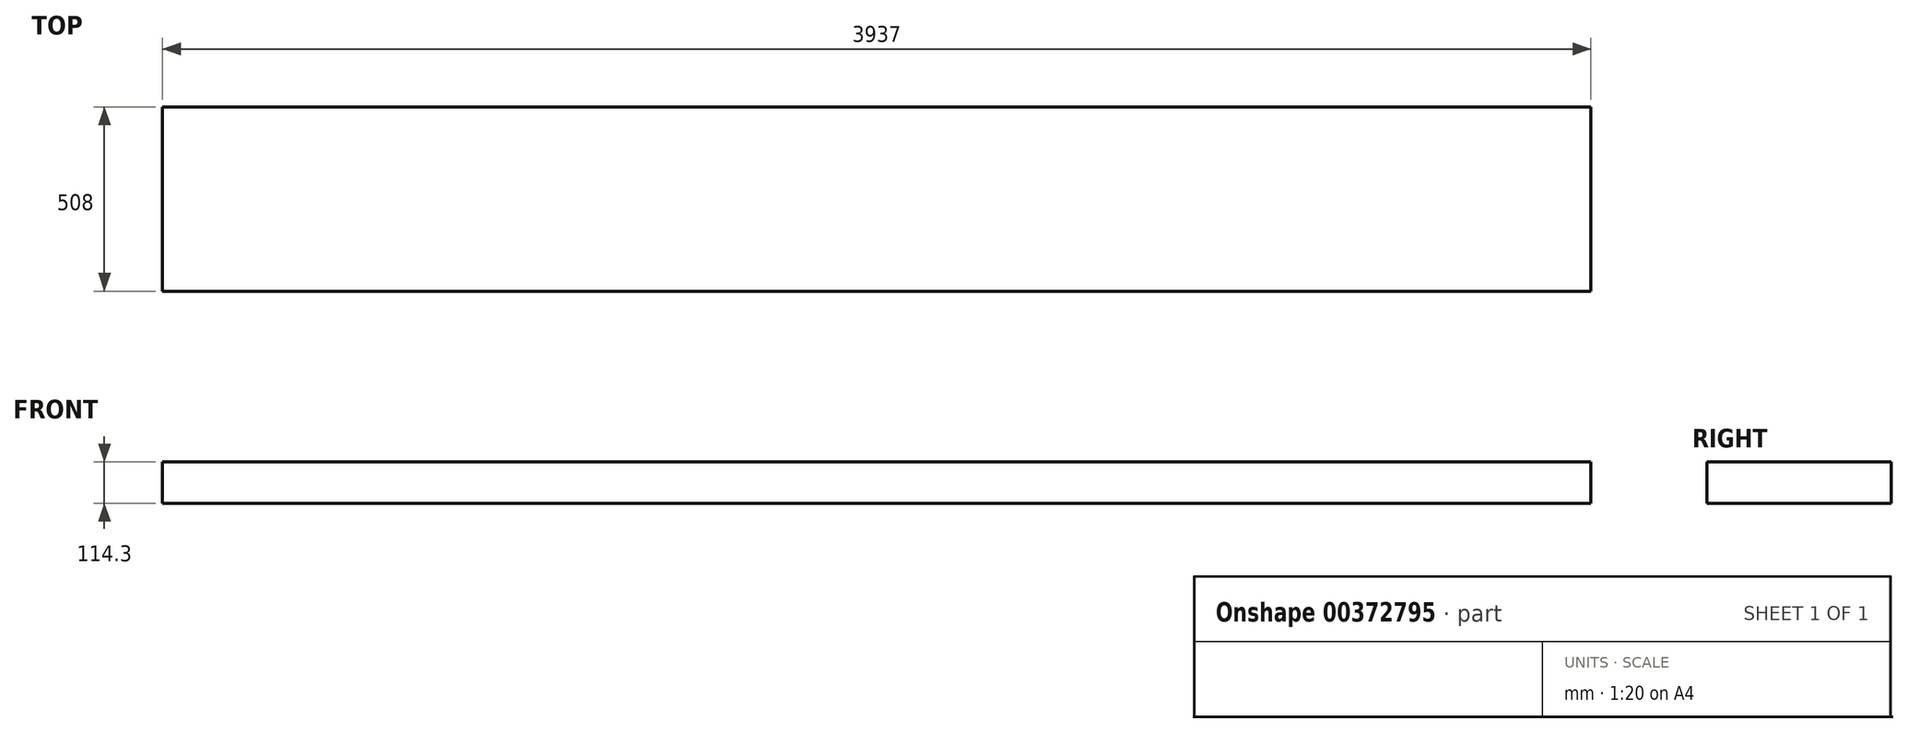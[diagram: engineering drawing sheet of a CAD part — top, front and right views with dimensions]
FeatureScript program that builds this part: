
annotation { "Feature Type Name" : "Feature", "Feature Type Description" : "" }
export const myFeature = defineFeature(function(context is Context, id is Id, definition is map)
    precondition{}
    {
        {
            var Q0;
            Q0=qCreatedBy(makeId("Top.planeOp"),FACE);
            var sketch = newSketch(context, id + "F0", { "sketchPlane" : qUnion([Q0])});
            skLineSegment(sketch, "E0.bottom", {"start": v(-1974.88, -417.26) * mm, "end": v(1962.12, -417.26) * mm});
            skLineSegment(sketch, "E0.top", {"start": v(-1974.88, -925.26) * mm, "end": v(1962.12, -925.26) * mm});
            skLineSegment(sketch, "E0.left", {"start": v(-1974.88, -417.26) * mm, "end": v(-1974.88, -925.26) * mm});
            skLineSegment(sketch, "E0.right", {"start": v(1962.12, -417.26) * mm, "end": v(1962.12, -925.26) * mm});
            skSolve(sketch);
        }
        {
            var Q0;
            Q0=makeQuery(id+"F0.imprint","IMPRINT",FACE,{"disambiguationData":[TD([[makeQuery(id+"F0.imprint","IMPRINT",EDGE,{"derivedFrom":sQuery(id+"F0.wireOp",EDGE,"E0.bottom")}),-1.0]])]});
            extrude(context, id + "F1", {"entities" : qUnion([Q0]), "depth" : 114.3 * mm});
        }
    });
